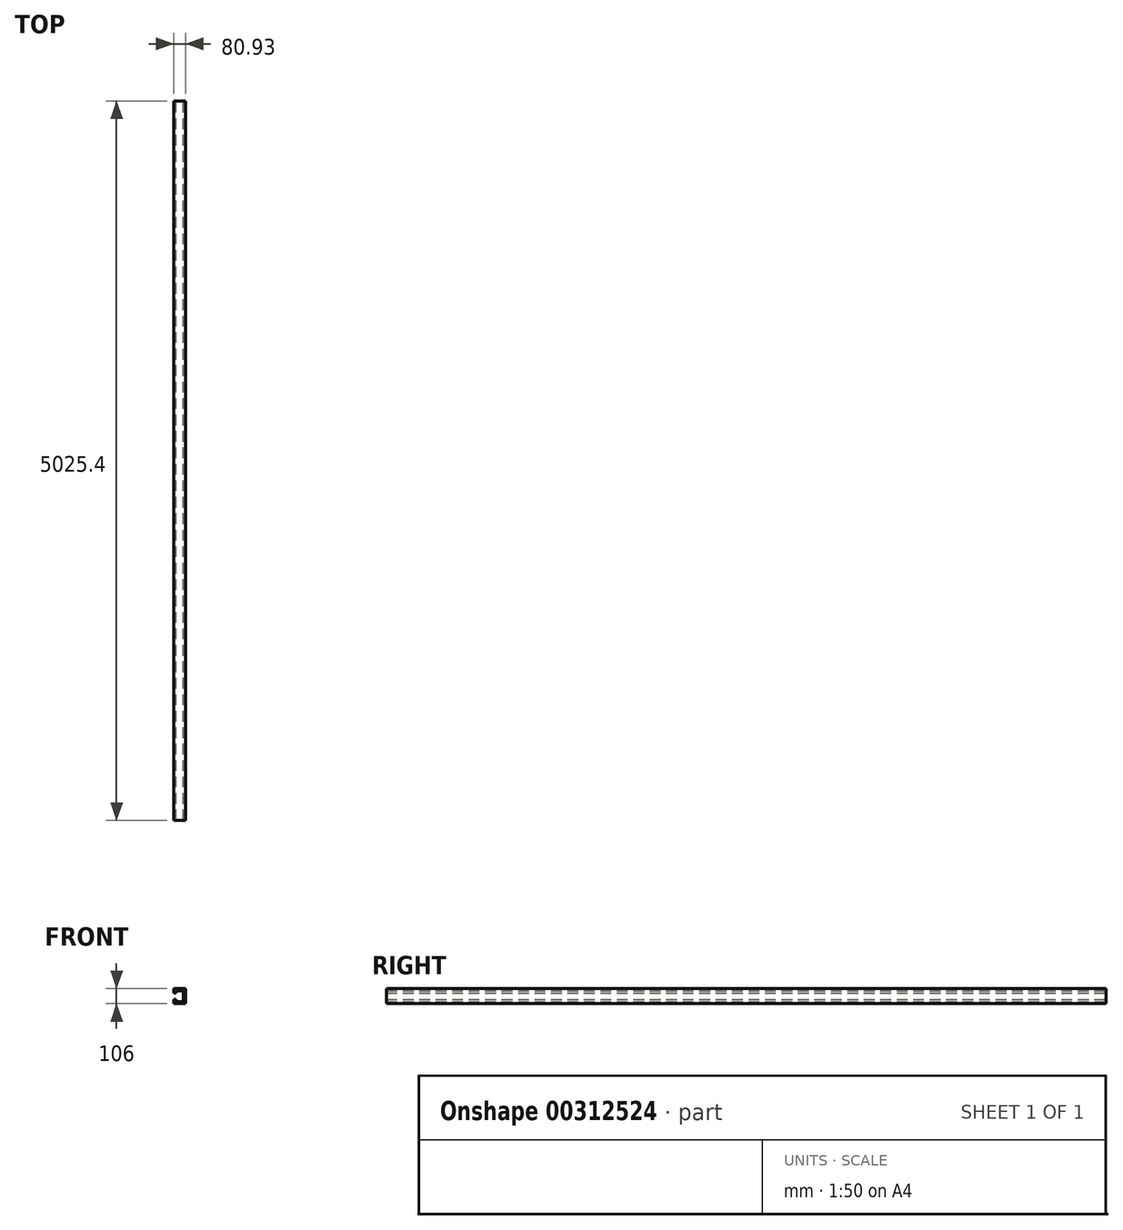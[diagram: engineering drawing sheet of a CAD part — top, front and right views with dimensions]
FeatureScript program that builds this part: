
annotation { "Feature Type Name" : "Feature", "Feature Type Description" : "" }
export const myFeature = defineFeature(function(context is Context, id is Id, definition is map)
    precondition{}
    {
        {
            var Q0;
            Q0=qCreatedBy(makeId("Front.planeOp"),FACE);
            var sketch = newSketch(context, id + "F0", { "sketchPlane" : qUnion([Q0])});
            skLineSegment(sketch, "E0.bottom", {"start": v(-33.33, 54.45) * mm, "end": v(47.6, 54.45) * mm});
            skLineSegment(sketch, "E0.top", {"start": v(-33.33, -51.55) * mm, "end": v(47.6, -51.55) * mm});
            skLineSegment(sketch, "E0.left", {"start": v(-33.33, 54.45) * mm, "end": v(-33.33, -51.55) * mm});
            skLineSegment(sketch, "E0.right", {"start": v(47.6, 54.45) * mm, "end": v(47.6, -51.55) * mm});
            skLineSegment(sketch, "E1.bottom", {"start": v(-17.14, 38.78) * mm, "end": v(33.5, 38.78) * mm});
            skLineSegment(sketch, "E1.top", {"start": v(-17.14, -39.02) * mm, "end": v(33.5, -39.02) * mm});
            skLineSegment(sketch, "E1.left", {"start": v(-17.14, 38.78) * mm, "end": v(-17.14, -39.02) * mm});
            skLineSegment(sketch, "E1.right", {"start": v(33.5, 38.78) * mm, "end": v(33.5, -39.02) * mm});
            skLineSegment(sketch, "E2", {"start": v(-17.14, -21.79) * mm, "end": v(-33.33, -21.79) * mm});
            skLineSegment(sketch, "E3", {"start": v(-17.14, 23.64) * mm, "end": v(-33.33, 23.64) * mm});
            skLineSegment(sketch, "E4", {"start": v(-33.33, 23.64) * mm, "end": v(-33.33, 54.45) * mm});
            skLineSegment(sketch, "E5", {"start": v(-33.33, 23.64) * mm, "end": v(-17.14, 23.64) * mm});
            skSolve(sketch);
        }
        {
            var Q0;
            Q0=makeQuery(id+"F0.imprint","IMPRINT",FACE,{"disambiguationData":[TD([[makeQuery(id+"F0.imprint","IMPRINT",EDGE,{"derivedFrom":sQuery(id+"F0.wireOp",EDGE,"E0.bottom")}),-1.0]])]});
            extrude(context, id + "F1", {"entities" : qUnion([Q0]), "depth" : 25.4 * mm});
        }
        {
            var Q0;
            Q0=makeQuery(id+"F1.opExtrude","CAP_FACE",FACE,{"disambiguationData":[OSD([sQuery(id+"F0.wireOp",EDGE,"E0.bottom"),sQuery(id+"F0.wireOp",EDGE,"E0.top"),sQuery(id+"F0.wireOp",EDGE,"E0.left"),sQuery(id+"F0.wireOp",EDGE,"E0.right"),sQuery(id+"F0.wireOp",EDGE,"E1.top"),sQuery(id+"F0.wireOp",EDGE,"E1.left"),sQuery(id+"F0.wireOp",EDGE,"E1.right"),sQuery(id+"F0.wireOp",EDGE,"E2"),sQuery(id+"F0.wireOp",EDGE,"E4"),sQuery(id+"F0.wireOp",EDGE,"E5"),sQuery(id+"F0.wireOp",EDGE,"E1.bottom")])],"isStart":true});
            extrude(context, id + "F2", {"entities" : qUnion([Q0]), "operationType" : NewBodyOperationType.ADD, "depth" : 5000 * mm});
        }
    });
